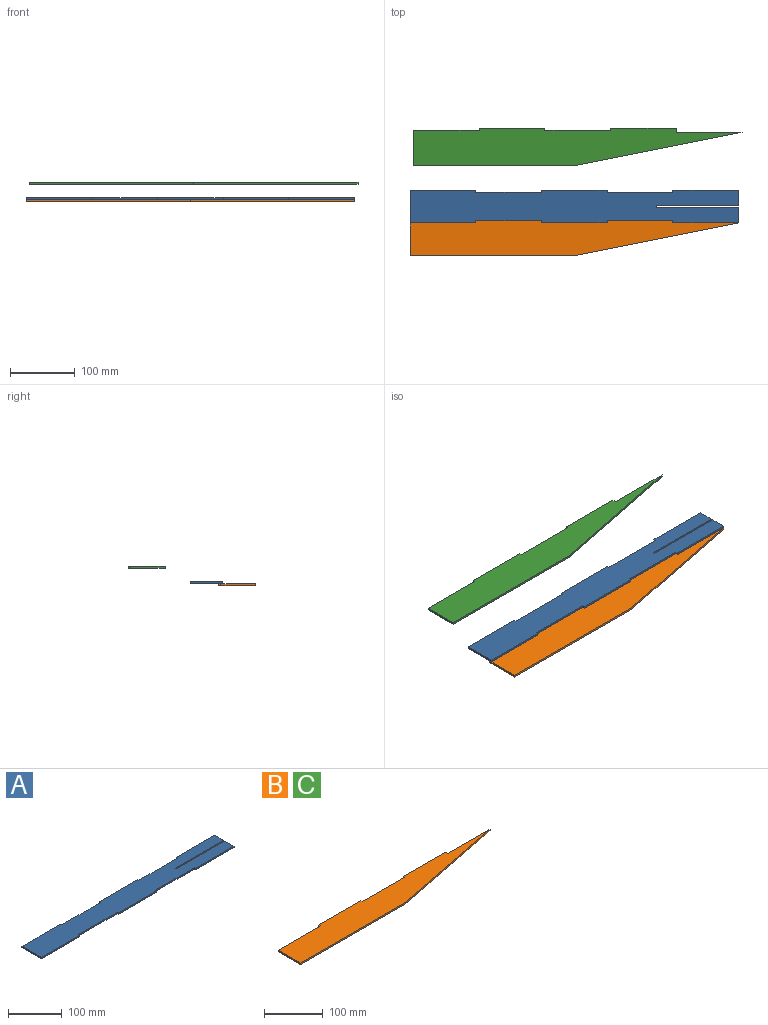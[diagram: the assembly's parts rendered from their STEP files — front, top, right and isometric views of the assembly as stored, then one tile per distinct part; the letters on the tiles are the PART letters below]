
ASSEMBLY  parts=3 mates=1
PART A: 26 faces, bbox 508x50.8x3.2 mm
  f0: plane 23.81x3.18mm, normal (1,0,0), area 75.6mm2, adj f2,f3,f4,f23
  f1: plane 101.6x3.18mm, normal (0,1,0), area 322.6mm2, adj f3,f4,f18,f20
  f2: plane 101.6x3.18mm, normal (0,1,0), area 322.6mm2, adj f0,f3,f4,f17
  f3: plane 508x50.8mm, normal (0,0,1), area 24112.9mm2, adj f0,f1,f2,f5,f6,f7,f8,f9
  f4: plane 508x50.8mm, normal (0,0,-1), area 24112.9mm2, adj f0,f1,f2,f5,f6,f7,f8,f9
  f5: plane 101.6x3.18mm, normal (0,-1,0), area 322.6mm2, adj f3,f4,f13,f14
  f6: plane 101.6x3.18mm, normal (0,-1,0), area 322.6mm2, adj f3,f4,f10,f11
  f7: plane 101.6x3.18mm, normal (0,1,0), area 322.6mm2, adj f3,f4,f8,f21
  f8: plane 50.8x3.18mm, normal (-1,0,0), area 161.3mm2, adj f3,f4,f7,f9
  f9: plane 101.6x3.18mm, normal (0,-1,0), area 322.6mm2, adj f3,f4,f8,f16
  f10: plane 23.81x3.18mm, normal (1,0,0), area 75.6mm2, adj f3,f4,f6,f25
  f11: plane 3.18x3.18mm, normal (-1,0,0), area 10.1mm2, adj f3,f4,f6,f12
  f12: plane 101.6x3.18mm, normal (0,-1,0), area 322.6mm2, adj f3,f4,f11,f13
  f13: plane 3.18x3.18mm, normal (1,0,0), area 10.1mm2, adj f3,f4,f5,f12
  f14: plane 3.18x3.18mm, normal (-1,0,0), area 10.1mm2, adj f3,f4,f5,f15
  f15: plane 101.6x3.18mm, normal (0,-1,0), area 322.6mm2, adj f3,f4,f14,f16
  f16: plane 3.18x3.18mm, normal (1,0,0), area 10.1mm2, adj f3,f4,f9,f15
  f17: plane 3.18x3.18mm, normal (-1,0,0), area 10.1mm2, adj f2,f3,f4,f19
  f18: plane 3.18x3.18mm, normal (1,0,0), area 10.1mm2, adj f1,f3,f4,f19
  f19: plane 101.6x3.18mm, normal (0,1,0), area 322.6mm2, adj f3,f4,f17,f18
  f20: plane 3.18x3.18mm, normal (-1,0,0), area 10.1mm2, adj f1,f3,f4,f22
  f21: plane 3.18x3.18mm, normal (1,0,0), area 10.1mm2, adj f3,f4,f7,f22
  f22: plane 101.6x3.18mm, normal (0,1,0), area 322.6mm2, adj f3,f4,f20,f21
  f23: plane 127x3.18mm, normal (0,-1,0), area 403.2mm2, adj f0,f3,f4,f24
  f24: plane 3.18x3.18mm, normal (1,0,0), area 10.1mm2, adj f3,f4,f23,f25
  f25: plane 127x3.18mm, normal (0,1,0), area 403.2mm2, adj f3,f4,f10,f24
PART B: 14 faces, bbox 508x57.2x3.2 mm
  f0: plane 508x57.15mm, normal (0,0,1), area 21290.3mm2, adj f2,f3,f4,f5,f6,f7,f8,f9
  f1: plane 508x57.15mm, normal (0,0,-1), area 21290.3mm2, adj f2,f3,f4,f5,f6,f7,f8,f9
  f2: plane 101.6x3.18mm, normal (0,1,0), area 322.6mm2, adj f0,f1,f10,f12
  f3: plane 101.6x3.18mm, normal (0,1,0), area 322.6mm2, adj f0,f1,f7,f9
  f4: plane 53.98x3.18mm, normal (-1,0,0), area 171.4mm2, adj f0,f1,f5,f11
  f5: plane 254x3.18mm, normal (0,-1,0), area 806.4mm2, adj f0,f1,f4,f6
  f6: plane 254x50.8mm, normal (0.2,-0.98,0), area 822.4mm2, adj f0,f1,f5,f13
  f7: plane 6.35x3.18mm, normal (1,0,0), area 20.2mm2, adj f0,f1,f3,f13
  f8: plane 101.6x3.18mm, normal (0,1,0), area 322.6mm2, adj f0,f1,f9,f10
  f9: plane 3.18x3.18mm, normal (-1,0,0), area 10.1mm2, adj f0,f1,f3,f8
  f10: plane 3.18x3.18mm, normal (1,0,0), area 10.1mm2, adj f0,f1,f2,f8
  f11: plane 101.6x3.18mm, normal (0,1,0), area 322.6mm2, adj f0,f1,f4,f12
  f12: plane 3.18x3.18mm, normal (-1,0,0), area 10.1mm2, adj f0,f1,f2,f11
  f13: plane 101.6x3.18mm, normal (0,1,0), area 322.6mm2, adj f0,f1,f6,f7
PART C: same geometry as B
PLACE A t=(-44.52,77.12,-97.48)mm
PLACE B t=(-44.52,26.32,-100.66)mm
PLACE C t=(-39.08,166.45,-73.31)mm
MATE fastened A.f16 <-> B.f12  axis (1,0,0) through (57.08,80.3,-97.48)mm
